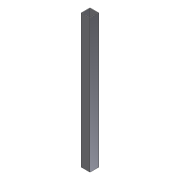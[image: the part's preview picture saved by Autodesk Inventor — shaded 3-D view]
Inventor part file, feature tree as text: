
AUTODESK INVENTOR PART (.ipt)
format: ipt  version: 2012 (Build 160160000, 160)  size: 71,680 bytes
history: native  units: in
note: dims shown in document units (in); Inventor stores cm internally (conversion verified against a paired STEP export)
features: extrude x1, shell x1, sketch x1
ambient origin geometry x8: Origin, YZ Plane, XZ Plane, XY Plane, X Axis, Y Axis, Z Axis, Center Point
bodies: Solid1 (feature_tree)
feature tree (3):
  extrude  "Extrusion1"  Depth=15.0in
  shell  "Shell2"  Thickness=1.0in
  sketch  "Sketch1"  dims[d0=1.0in d1=15.0in d2=1.0in d3=0.0in d5=0.0625in]
